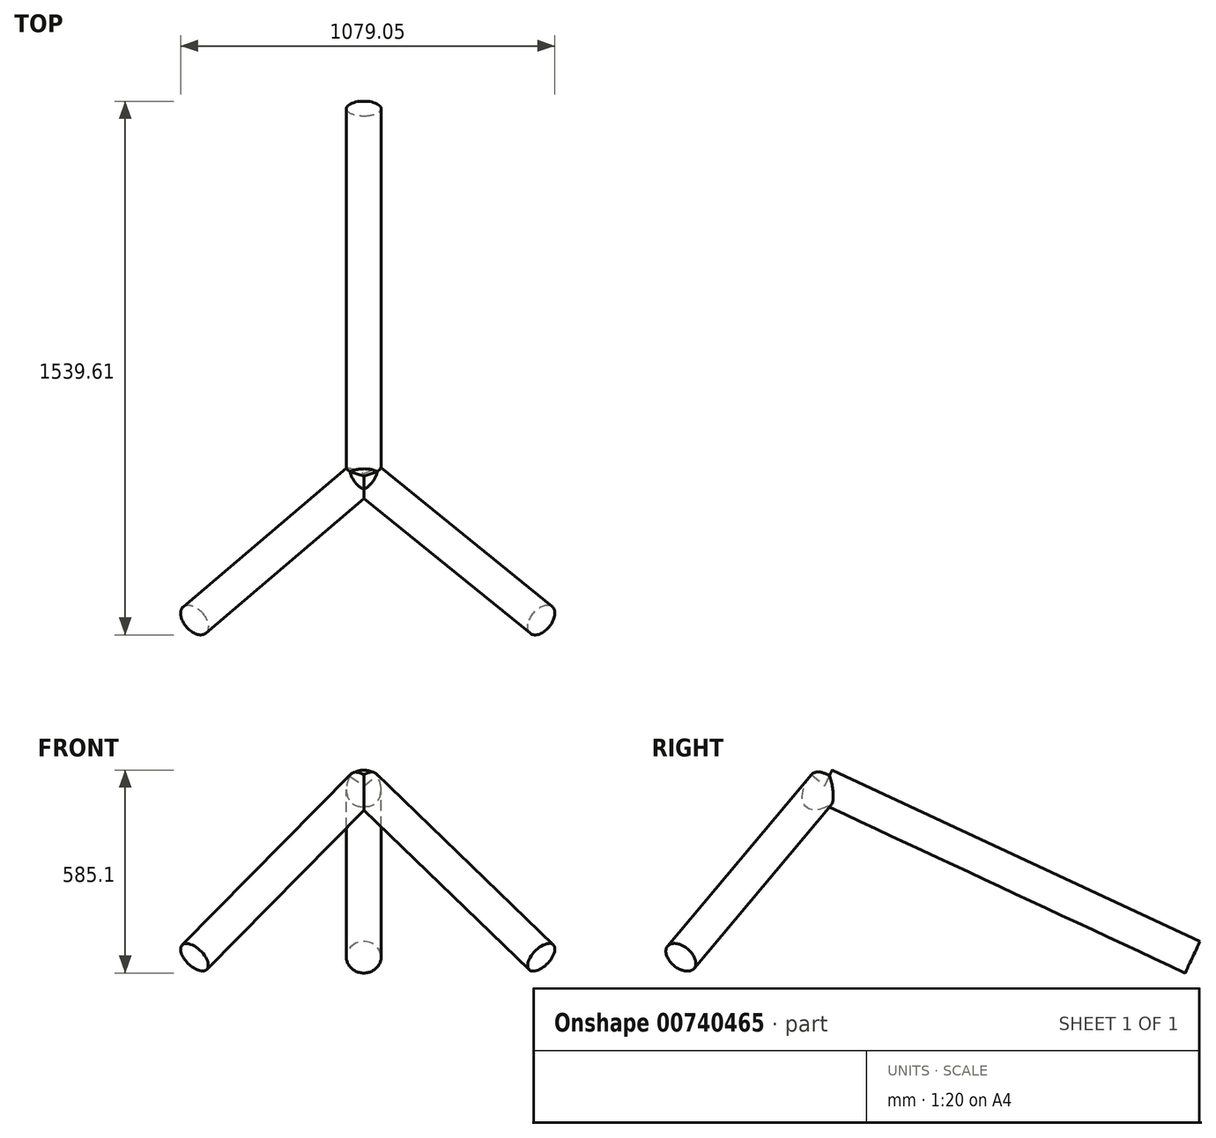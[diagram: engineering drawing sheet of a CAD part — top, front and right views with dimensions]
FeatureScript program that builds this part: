
annotation { "Feature Type Name" : "Feature", "Feature Type Description" : "" }
export const myFeature = defineFeature(function(context is Context, id is Id, definition is map)
    precondition{}
    {
        {
            var Q0;
            Q0=qCreatedBy(makeId("Right.planeOp"),FACE);
            var sketch = newSketch(context, id + "F0", { "sketchPlane" : qUnion([Q0])});
            skLineSegment(sketch, "E0", {"start": v(821.65, 0) * mm, "end": v(-238.73, 494.46) * mm});
            skLineSegment(sketch, "E1", {"start": v(821.65, 0) * mm, "end": v(-653.64, 0) * mm, "construction": true});
            skLineSegment(sketch, "E2", {"start": v(-238.73, 494.46) * mm, "end": v(-653.64, 0) * mm, "construction": true});
            skSolve(sketch);
        }
        {
            var Q0;
            Q0=qCreatedBy(makeId("Top.planeOp"),FACE);
            var sketch = newSketch(context, id + "F1", { "sketchPlane" : qUnion([Q0])});
            skLineSegment(sketch, "E3", {"start": v(-488.14, -653.64) * mm, "end": v(511.85, -653.64) * mm, "construction": true});
            skCircle(sketch, "E4", {"center": v(-438.15, -653) * mm, "radius": 50 * mm});
            skCircle(sketch, "E5", {"center": v(461.86, -652.97) * mm, "radius": 50 * mm});
            skPoint(sketch, "E6.0", {"position": v(0, 772.08) * mm});
            skCircle(sketch, "E7", {"center": v(0, 772.08) * mm, "radius": 49.57 * mm});
            skSolve(sketch);
        }
        {
            var Q0;
            Q0=sQuery(id+"F0.wireOp",VERTEX,"E0.end");
            var Q1;
            Q1=sQuery(id+"F1.wireOp",VERTEX,"E3.start");
            var Q2;
            Q2=sQuery(id+"F0.wireOp",VERTEX,"E1.end");
            cPlane(context, id + "F2", {"entities" : qUnion([Q0, Q1, Q2]), "cplaneType" : CPlaneType.THREE_POINT, "offset" : 25 * mm, "width" : 150 * mm, "height" : 150 * mm});
        }
        {
            var Q0;
            Q0=qCreatedBy(id+"F2.planeOp",FACE);
            var sketch = newSketch(context, id + "F3", { "sketchPlane" : qUnion([Q0])});
            skPoint(sketch, "E8.0", {"position": v(0, 225.33) * mm});
            skPoint(sketch, "E9.0", {"position": v(488.14, -420.15) * mm});
            skLineSegment(sketch, "E10", {"start": v(0, 225.33) * mm, "end": v(488.14, -420.15) * mm});
            skSolve(sketch);
        }
        {
            var Q0;
            Q0=sQuery(id+"F3.wireOp",VERTEX,"E8.0");
            var Q1;
            Q1=sQuery(id+"F0.wireOp",VERTEX,"E1.end");
            var Q2;
            Q2=sQuery(id+"F1.wireOp",VERTEX,"E3.end");
            cPlane(context, id + "F4", {"entities" : qUnion([Q0, Q1, Q2]), "cplaneType" : CPlaneType.THREE_POINT, "offset" : 25 * mm, "width" : 150 * mm, "height" : 150 * mm});
        }
        {
            var Q0;
            Q0=qCreatedBy(id+"F4.planeOp",FACE);
            var sketch = newSketch(context, id + "F5", { "sketchPlane" : qUnion([Q0])});
            skPoint(sketch, "E11.0", {"position": v(0, 225.33) * mm});
            skPoint(sketch, "E12.0", {"position": v(-511.85, -420.15) * mm});
            skLineSegment(sketch, "E13", {"start": v(0, 225.33) * mm, "end": v(-511.85, -420.15) * mm});
            skSolve(sketch);
        }
        {
            var Q0;
            Q0=sQuery(id+"F3.wireOp",EDGE,"E10");
            var Q1;
            Q1=sQuery(id+"F3.wireOp",VERTEX,"E9.0");
            cPlane(context, id + "F6", {"entities" : qUnion([Q0, Q1]), "cplaneType" : CPlaneType.LINE_POINT, "offset" : 25 * mm, "width" : 150 * mm, "height" : 150 * mm});
        }
        {
            var Q0;
            Q0=qCreatedBy(id+"F6.planeOp",FACE);
            var sketch = newSketch(context, id + "F7", { "sketchPlane" : qUnion([Q0])});
            skPoint(sketch, "E14.0", {"position": v(-135.91, 500.71) * mm});
            skCircle(sketch, "E15", {"center": v(-135.91, 500.71) * mm, "radius": 50 * mm});
            skSolve(sketch);
        }
        {
            var Q0;
            Q0=sQuery(id+"F5.wireOp",EDGE,"E13");
            var Q1;
            Q1=sQuery(id+"F5.wireOp",VERTEX,"E12.0");
            cPlane(context, id + "F8", {"entities" : qUnion([Q0, Q1]), "cplaneType" : CPlaneType.LINE_POINT, "offset" : 25 * mm, "width" : 150 * mm, "height" : 150 * mm});
        }
        {
            var Q0;
            Q0=qCreatedBy(id+"F8.planeOp",FACE);
            var sketch = newSketch(context, id + "F9", { "sketchPlane" : qUnion([Q0])});
            skPoint(sketch, "E16.0", {"position": v(-379.27, 355.63) * mm});
            skCircle(sketch, "E17", {"center": v(-379.27, 355.63) * mm, "radius": 50 * mm});
            skSolve(sketch);
        }
        {
            var Q0;
            Q0=sQuery(id+"F0.wireOp",EDGE,"E0");
            var Q1;
            Q1=sQuery(id+"F0.wireOp",VERTEX,"E0.start");
            cPlane(context, id + "F10", {"entities" : qUnion([Q0, Q1]), "cplaneType" : CPlaneType.LINE_POINT, "offset" : 25 * mm, "width" : 150 * mm, "height" : 150 * mm});
        }
        {
            var Q0;
            Q0=qCreatedBy(id+"F10.planeOp",FACE);
            var sketch = newSketch(context, id + "F11", { "sketchPlane" : qUnion([Q0])});
            skPoint(sketch, "E18.0", {"position": v(0, 347.24) * mm});
            skCircle(sketch, "E19", {"center": v(0, 347.24) * mm, "radius": 50 * mm});
            skSolve(sketch);
        }
        {
            var Q0;
            Q0=makeQuery(id+"F11.imprint","IMPRINT",FACE,{"disambiguationData":[TD([[makeQuery(id+"F11.imprint","IMPRINT",EDGE,{"derivedFrom":sQuery(id+"F11.wireOp",EDGE,"E19")}),1.0]])]});
            var Q1;
            Q1=sQuery(id+"F0.wireOp",EDGE,"E0");
            sweep(context, id + "F12", {"profiles" : qUnion([Q0]), "path" : qUnion([Q1])});
        }
        {
            var Q0;
            Q0=makeQuery(id+"F9.imprint","IMPRINT",FACE,{"disambiguationData":[TD([[makeQuery(id+"F9.imprint","IMPRINT",EDGE,{"derivedFrom":sQuery(id+"F9.wireOp",EDGE,"E17")}),1.0]])]});
            var Q1;
            Q1=sQuery(id+"F5.wireOp",EDGE,"E13");
            sweep(context, id + "F13", {"operationType" : NewBodyOperationType.ADD, "profiles" : qUnion([Q0]), "path" : qUnion([Q1])});
        }
        {
            var Q0;
            Q0=makeQuery(id+"F7.imprint","IMPRINT",FACE,{"disambiguationData":[TD([[makeQuery(id+"F7.imprint","IMPRINT",EDGE,{"derivedFrom":sQuery(id+"F7.wireOp",EDGE,"E15")}),1.0]])]});
            var Q1;
            Q1=sQuery(id+"F3.wireOp",EDGE,"E10");
            sweep(context, id + "F14", {"operationType" : NewBodyOperationType.ADD, "profiles" : qUnion([Q0]), "path" : qUnion([Q1])});
        }
    });
